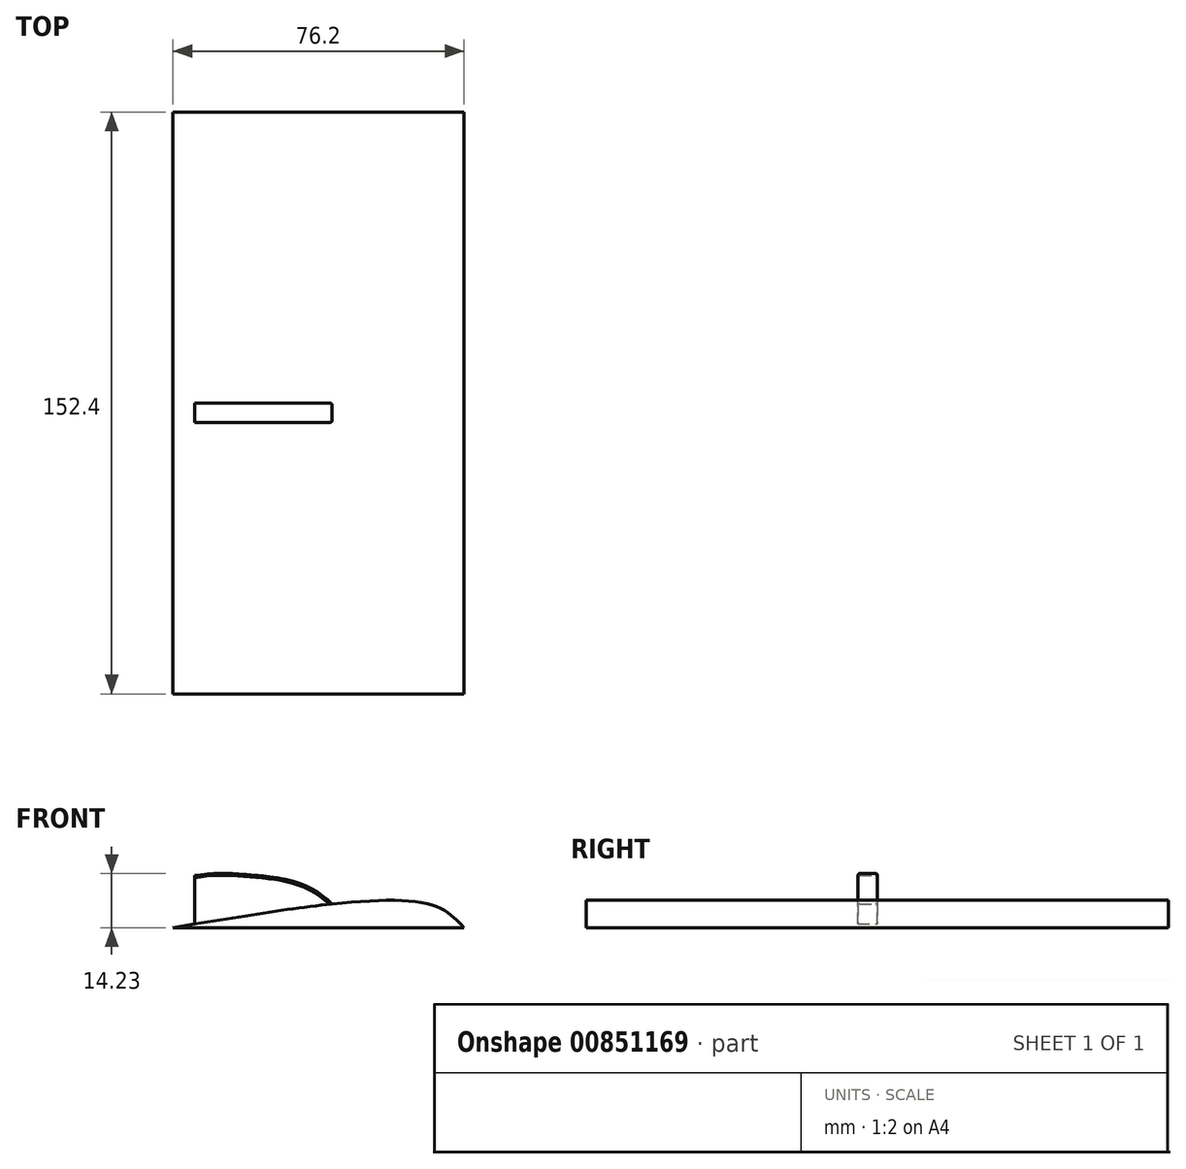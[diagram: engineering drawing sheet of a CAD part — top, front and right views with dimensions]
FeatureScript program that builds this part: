
annotation { "Feature Type Name" : "Feature", "Feature Type Description" : "" }
export const myFeature = defineFeature(function(context is Context, id is Id, definition is map)
    precondition{}
    {
        {
            var Q0;
            Q0=qCreatedBy(makeId("Front.planeOp"),FACE);
            var sketch = newSketch(context, id + "F0", { "sketchPlane" : qUnion([Q0])});
            skLineSegment(sketch, "E0", {"start": v(-41.65, 0) * mm, "end": v(34.55, 0) * mm});
            skFitSpline(sketch, "E1", {"points": [v(34.55, 0) * mm, v(25.08, 6.24) * mm, v(-41.65, 0) * mm], "startDerivative": vector(-23.5, 25.82) * mm, "endDerivative": vector(-116.03, -19.52) * mm});
            skLineSegment(sketch, "E2", {"start": v(-35.97, 0.95) * mm, "end": v(-35.97, 13.65) * mm});
            skFitSpline(sketch, "E3", {"points": [v(-35.97, 13.65) * mm, v(-19.27, 13.65) * mm, v(0, 6.24) * mm], "startDerivative": vector(37.16, 6.1) * mm, "endDerivative": vector(34.84, -34.19) * mm});
            skSolve(sketch);
        }
        {
            var Q0;
            {var subQ0=sQuery(id+"F0.wireOp",EDGE,"E2");Q0=makeQuery(id+"F0.imprint","IMPRINT",FACE,{"disambiguationData":[TD([[makeQuery(id+"F0.imprint","IMPRINT",EDGE,{"derivedFrom":subQ0}),-1.0]])]});}
            var sketch = newSketch(context, id + "F1", { "sketchPlane" : qUnion([Q0])});
            skSolve(sketch);
        }
        {
            var Q0;
            {var subQ0=sQuery(id+"F0.wireOp",EDGE,"E0");Q0=makeQuery(id+"F0.imprint","IMPRINT",FACE,{"disambiguationData":[TD([[makeQuery(id+"F0.imprint","IMPRINT",EDGE,{"derivedFrom":subQ0}),1.0]])]});}
            extrude(context, id + "F2", {"entities" : qUnion([Q0]), "endBound" : BoundingType.SYMMETRIC, "depth" : 152.4 * mm, "offsetDistance" : 25.4 * mm});
        }
        {
            var Q0;
            {var subQ0=sQuery(id+"F0.wireOp",EDGE,"E2");Q0=makeQuery(id+"F1.imprint","IMPRINT",FACE,{"disambiguationData":[TD([[makeQuery(id+"F1.imprint","IMPRINT",EDGE,{"derivedFrom":makeQuery(id+"F0.imprint","IMPRINT",EDGE,{"derivedFrom":subQ0})}),-1.0]])]});}
            extrude(context, id + "F3", {"entities" : qUnion([Q0]), "operationType" : NewBodyOperationType.ADD, "depth" : 5.08 * mm, "offsetDistance" : 25.4 * mm});
        }
        {
            var Q0;
            Q0=makeQuery(id+"F3.opExtrude","CAP_EDGE",EDGE,{"disambiguationData":[OSD([sQuery(id+"F0.wireOp",EDGE,"E3")])],"isStart":true});
            fillet(context, id + "F4", {"entities" : qUnion([Q0]), "radius" : 0.5 * mm, "tangentPropagation" : true, "allowEdgeOverflow" : false});
        }
        {
            var Q0;
            Q0=makeQuery(id+"F3.opExtrude","CAP_EDGE",EDGE,{"disambiguationData":[OSD([sQuery(id+"F0.wireOp",EDGE,"E3")])],"isStart":false});
            fillet(context, id + "F5", {"entities" : qUnion([Q0]), "radius" : 0.5 * mm, "tangentPropagation" : true, "allowEdgeOverflow" : false});
        }
    });
